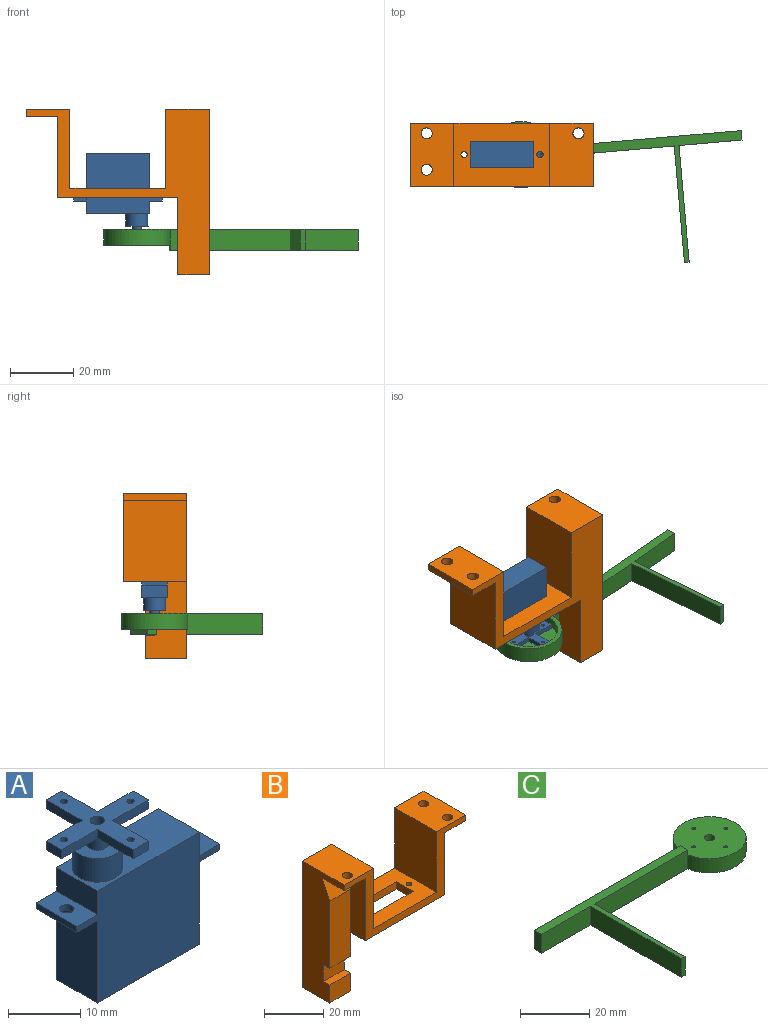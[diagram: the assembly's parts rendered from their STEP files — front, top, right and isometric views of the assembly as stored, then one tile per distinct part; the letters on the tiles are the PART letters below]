
ASSEMBLY  parts=3 mates=2
PART A: 41 faces, bbox 28.5x17x27 mm
  f0: plane 8x4mm, normal (-1,0,0), area 32mm2, adj f3,f5,f6,f16
  f1: plane 14x8mm, normal (1,0,0), area 112mm2, adj f3,f5,f7,f11
  f2: plane 14x8mm, normal (-1,0,0), area 112mm2, adj f3,f5,f7,f15
  f3: plane 24x19mm, normal (0,-1,0), area 384mm2, adj f0,f1,f2,f4,f6,f7,f10,f15
  f4: plane 8x4mm, normal (1,0,0), area 32mm2, adj f3,f5,f6,f13
  f5: plane 24x19mm, normal (0,1,0), area 384mm2, adj f0,f1,f2,f4,f6,f7,f12,f15
  f6: plane 20x8mm, normal (0,0,1), area 121.5mm2, adj f0,f3,f4,f5,f8
  f7: plane 20x8mm, normal (0,0,-1), area 160mm2, adj f1,f2,f3,f5
  f8: cylinder r=3.5mm len=7mm, axis (0,0,-1), area 88mm2, adj f6,f9
  f9: plane 7x7mm, normal (0,0,1), area 31.4mm2, adj f8,f18
  f10: plane 4x1mm, normal (0,-1,0), area 4mm2, adj f3,f11,f13,f14
  f11: plane 8x4mm, normal (0,0,-1), area 28.9mm2, adj f1,f10,f12,f14,f20
  f12: plane 4x1mm, normal (0,1,0), area 4mm2, adj f5,f11,f13,f14
  f13: plane 8x4mm, normal (0,0,1), area 28.9mm2, adj f4,f10,f12,f14,f20
  f14: plane 8x1mm, normal (1,0,0), area 8mm2, adj f10,f11,f12,f13
  f15: plane 8x4mm, normal (0,0,-1), area 28.9mm2, adj f2,f3,f5,f17,f19
  f16: plane 8x4mm, normal (0,0,1), area 28.9mm2, adj f0,f3,f5,f17,f19
  f17: plane 8x1mm, normal (-1,0,0), area 8mm2, adj f3,f5,f15,f16
  f18: cylinder r=1.5mm len=3mm, axis (0,0,-1), area 23.6mm2, adj f9,f34
  f19: cylinder r=1mm len=2mm, axis (0,0,1), area 6.3mm2, adj f15,f16
  f20: cylinder r=1mm len=2mm, axis (0,0,1), area 6.3mm2, adj f11,f13
  f21: plane 7x1.5mm, normal (0,1,0), area 10.5mm2, adj f22,f32,f33,f34
  f22: plane 3x1.5mm, normal (-1,0,0), area 4.5mm2, adj f21,f23,f33,f34
  f23: plane 7x1.5mm, normal (0,-1,0), area 10.5mm2, adj f22,f24,f33,f34
  f24: plane 7x1.5mm, normal (-1,0,0), area 10.5mm2, adj f23,f25,f33,f34
  f25: plane 3x1.5mm, normal (0,-1,0), area 4.5mm2, adj f24,f26,f33,f34
  f26: plane 7x1.5mm, normal (1,0,0), area 10.5mm2, adj f25,f27,f33,f34
  f27: plane 7x1.5mm, normal (0,-1,0), area 10.5mm2, adj f26,f28,f33,f34
  f28: plane 3x1.5mm, normal (1,0,0), area 4.5mm2, adj f27,f29,f33,f34
  f29: plane 7x1.5mm, normal (0,1,0), area 10.5mm2, adj f28,f30,f33,f34
  f30: plane 7x1.5mm, normal (1,0,0), area 10.5mm2, adj f29,f31,f33,f34
  f31: plane 3x1.5mm, normal (0,1,0), area 4.5mm2, adj f30,f32,f33,f34
  f32: plane 7x1.5mm, normal (-1,0,0), area 10.5mm2, adj f21,f31,f33,f34
  f33: plane 17x17mm, normal (0,0,1), area 86.7mm2, adj f21,f22,f23,f24,f25,f26,f27,f28
  f34: plane 17x17mm, normal (0,0,-1), area 82.8mm2, adj f18,f21,f22,f23,f24,f25,f26,f27
  f35: cylinder r=0.5mm len=1.5mm, axis (0,0,1), area 4.7mm2, adj f33,f34
  f36: cylinder r=0.5mm len=1.5mm, axis (0,0,1), area 4.7mm2, adj f33,f34
  f37: cylinder r=0.5mm len=1.5mm, axis (0,0,1), area 4.7mm2, adj f33,f34
  f38: cylinder r=0.5mm len=1.5mm, axis (0,0,1), area 4.7mm2, adj f33,f34
  f39: cylinder r=1mm len=2mm, axis (0,0,1), area 12.6mm2, adj f33,f40
  f40: plane 2x2mm, normal (0,0,1), area 3.1mm2, adj f39
PART B: 31 faces, bbox 58x19.9x52.3 mm
  f0: plane 52.3x19.93mm, normal (-1,0,0), area 661.1mm2, adj f1,f2,f5,f11,f14,f17,f26,f27
  f1: plane 27.75x10mm, normal (0,-1,0), area 277.5mm2, adj f0,f4,f25,f27,f30
  f2: plane 10x7.4mm, normal (0,-1,0), area 74mm2, adj f0,f25,f26,f29
  f3: plane 30.2x19.93mm, normal (0,0,1), area 435.7mm2, adj f5,f7,f8,f9,f10,f11,f13,f15
  f4: plane 25.7x10.47mm, normal (-1,0,0), area 192mm2, adj f1,f5,f12,f17,f30
  f5: plane 58x28mm, normal (0,-1,0), area 355.1mm2, adj f0,f3,f4,f6,f12,f13,f14,f15
  f6: plane 25.7x19.93mm, normal (1,0,0), area 512.3mm2, adj f5,f11,f12,f18
  f7: plane 8x3mm, normal (1,0,0), area 24mm2, adj f3,f8,f10,f12
  f8: plane 20x3mm, normal (0,-1,0), area 60mm2, adj f3,f7,f9,f12
  f9: plane 8x3mm, normal (-1,0,0), area 24mm2, adj f3,f8,f10,f12
  f10: plane 20x3mm, normal (0,1,0), area 60mm2, adj f3,f7,f9,f12
  f11: plane 58x52.3mm, normal (0,1,0), area 855.1mm2, adj f0,f3,f6,f12,f13,f14,f15,f16
  f12: plane 38x19.93mm, normal (0,0,-1), area 591.2mm2, adj f4,f5,f6,f7,f8,f9,f10,f11
  f13: plane 25x19.93mm, normal (1,0,0), area 498.4mm2, adj f3,f5,f11,f14
  f14: plane 19.93x13.9mm, normal (0,0,1), area 267.5mm2, adj f0,f5,f11,f13,f24
  f15: plane 25x19.93mm, normal (-1,0,0), area 498.4mm2, adj f3,f5,f11,f16
  f16: plane 19.93x13.9mm, normal (0,0,1), area 257.9mm2, adj f5,f11,f15,f19,f22,f23
  f17: plane 10.47x10mm, normal (0,0,-1), area 95mm2, adj f0,f4,f5,f24,f30
  f18: plane 19.93x10mm, normal (0,0,-1), area 180.1mm2, adj f5,f6,f11,f19,f22,f23
  f19: plane 19.93x2.3mm, normal (1,0,0), area 45.8mm2, adj f5,f11,f16,f18
  f20: cylinder r=1mm len=3mm, axis (0,0,-1), area 18.8mm2, adj f3,f12
  f21: cylinder r=1mm len=3mm, axis (0,0,-1), area 18.8mm2, adj f3,f12
  f22: cylinder r=1.75mm len=3.5mm, axis (0,0,-1), area 25.3mm2, adj f16,f18
  f23: cylinder r=1.75mm len=3.5mm, axis (0,0,-1), area 25.3mm2, adj f16,f18
  f24: cylinder r=1.75mm len=3.5mm, axis (0,0,-1), area 25.3mm2, adj f14,f17
  f25: plane 24.3x13mm, normal (1,0,0), area 295mm2, adj f1,f2,f11,f12,f26,f27,f28,f29
  f26: plane 13x10mm, normal (0,0,-1), area 130mm2, adj f0,f2,f11,f25
  f27: plane 10x3mm, normal (0,0,-1), area 30mm2, adj f0,f1,f25,f28
  f28: plane 10x7mm, normal (0,-1,0), area 70mm2, adj f0,f25,f27,f29
  f29: plane 10x3mm, normal (0,0,1), area 30mm2, adj f0,f2,f25,f28
  f30: plane 10x7.85mm, normal (0,-0.91,0.41), area 86.1mm2, adj f0,f1,f4,f17
PART C: 19 faces, bbox 80.5x49x6.6 mm
  f0: plane 38.11x6.6mm, normal (0,-1,0), area 251.5mm2, adj f2,f6,f14,f15,f17
  f1: plane 21x20.89mm, normal (0,0,1), area 335.9mm2, adj f2,f9,f10,f11,f12,f13,f14
  f2: cylinder r=10.5mm len=21mm, axis (0,0,-1), area 314.8mm2, adj f0,f1,f3,f6
  f3: plane 59.61x6.6mm, normal (0,1,0), area 393.4mm2, adj f2,f4,f6,f14,f15
  f4: plane 6.6x3mm, normal (-1,0,0), area 19.8mm2, adj f3,f5,f6,f15
  f5: plane 20x6.6mm, normal (0,-1,0), area 132mm2, adj f4,f6,f15,f16
  f6: plane 80.5x49mm, normal (0,0,-1), area 318.3mm2, adj f0,f2,f3,f4,f5,f7,f16,f17
  f7: cylinder r=9.14mm len=18.27mm, axis (0,0,-1), area 172.2mm2, adj f6,f8
  f8: plane 18.27x18.27mm, normal (0,0,-1), area 252mm2, adj f7,f9,f10,f11,f12,f13
  f9: cylinder r=0.5mm len=2mm, axis (0,0,-1), area 6.3mm2, adj f1,f8
  f10: cylinder r=0.5mm len=2mm, axis (0,0,-1), area 6.3mm2, adj f1,f8
  f11: cylinder r=0.5mm len=2mm, axis (0,0,-1), area 6.3mm2, adj f1,f8
  f12: cylinder r=1.5mm len=3mm, axis (0,0,-1), area 18.8mm2, adj f1,f8
  f13: cylinder r=0.5mm len=2mm, axis (0,0,-1), area 6.3mm2, adj f1,f8
  f14: plane 3x1.6mm, normal (1,0,0), area 4.8mm2, adj f0,f1,f3,f15
  f15: plane 59.61x40mm, normal (0,0,1), area 234.3mm2, adj f0,f3,f4,f5,f14,f16,f17,f18
  f16: plane 37x6.6mm, normal (-1,0,0), area 244.2mm2, adj f5,f6,f15,f18
  f17: plane 37x6.6mm, normal (1,0,0), area 244.2mm2, adj f0,f6,f15,f18
  f18: plane 6.6x1.5mm, normal (0,-1,0), area 9.9mm2, adj f6,f15,f16,f17
PLACE A rot(axis=(0,1,0),180deg) t=(-45.9,29.61,21.97)mm
PLACE B rot(axis=(0,0,1),180deg) t=(-34.24,24.35,7.97)mm
PLACE C rot(axis=(0.04,-1,0),180deg) t=(-28.14,23.81,-2.03)mm
MATE revolute C.f7 <-> A.f8  axis (0,0,1) through (-28.14,23.81,-5.03)mm
MATE fastened A.f20 <-> B.f20  axis (0,0,-1) through (-46.14,23.81,6.97)mm
